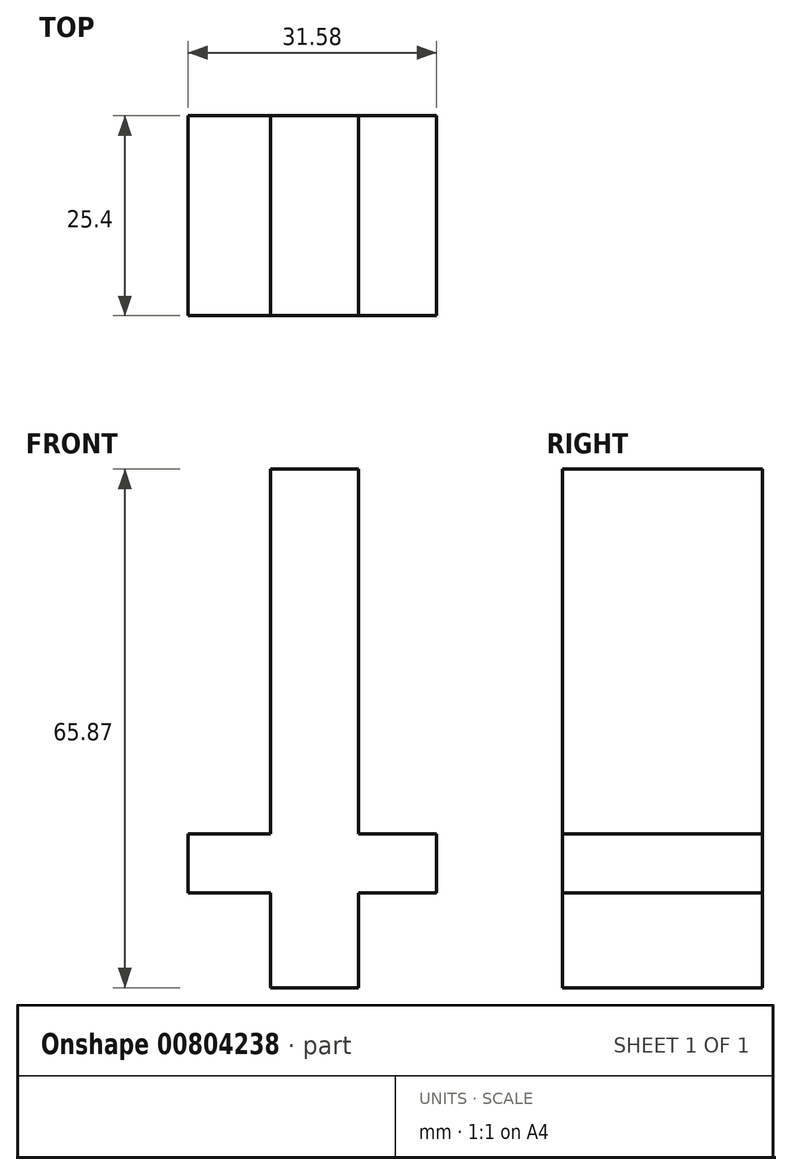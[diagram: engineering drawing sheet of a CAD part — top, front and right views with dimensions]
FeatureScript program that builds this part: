
annotation { "Feature Type Name" : "Feature", "Feature Type Description" : "" }
export const myFeature = defineFeature(function(context is Context, id is Id, definition is map)
    precondition{}
    {
        {
            var Q0;
            Q0=qCreatedBy(makeId("Front.planeOp"),FACE);
            var sketch = newSketch(context, id + "F0", { "sketchPlane" : qUnion([Q0])});
            skLineSegment(sketch, "E0.bottom", {"start": v(5.56, 23.91) * mm, "end": v(-5.56, 23.91) * mm});
            skLineSegment(sketch, "E0.top", {"start": v(5.56, -41.96) * mm, "end": v(-5.56, -41.96) * mm});
            skLineSegment(sketch, "E0.left", {"start": v(5.56, 23.91) * mm, "end": v(5.56, -41.96) * mm});
            skLineSegment(sketch, "E0.right", {"start": v(-5.56, 23.91) * mm, "end": v(-5.56, -41.96) * mm});
            skLineSegment(sketch, "E1.bottom", {"start": v(15.5, -29.93) * mm, "end": v(-16.1, -29.93) * mm});
            skLineSegment(sketch, "E1.top", {"start": v(15.5, -22.4) * mm, "end": v(-16.1, -22.4) * mm});
            skLineSegment(sketch, "E1.left", {"start": v(15.5, -29.93) * mm, "end": v(15.5, -22.4) * mm});
            skLineSegment(sketch, "E1.right", {"start": v(-16.1, -29.93) * mm, "end": v(-16.1, -22.4) * mm});
            skSolve(sketch);
        }
        {
            var Q0;
            Q0 = qSketchRegion(id + "F0", true);
            extrude(context, id + "F1", {"entities" : qUnion([Q0]), "depth" : 25.4 * mm, "offsetDistance" : 25.4 * mm});
        }
    });
